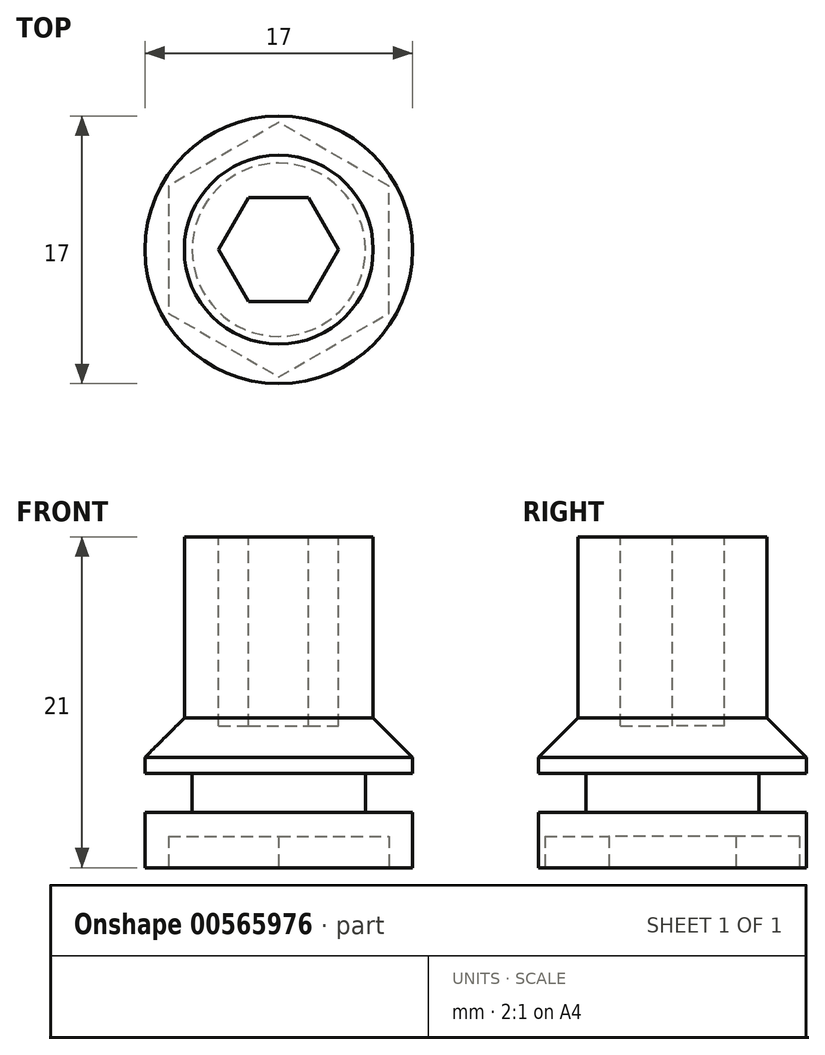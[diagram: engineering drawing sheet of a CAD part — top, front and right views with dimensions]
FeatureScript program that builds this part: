
annotation { "Feature Type Name" : "Feature", "Feature Type Description" : "" }
export const myFeature = defineFeature(function(context is Context, id is Id, definition is map)
    precondition{}
    {
        {
            var Q0;
            Q0=qCreatedBy(makeId("Top.planeOp"),FACE);
            var sketch = newSketch(context, id + "F0", { "sketchPlane" : qUnion([Q0])});
            skCircle(sketch, "E0", {"center": v(0, 0) * mm, "radius": 8.5 * mm});
            skSolve(sketch);
        }
        {
            var Q0;
            Q0=makeQuery(id+"F0.imprint","IMPRINT",FACE,{"disambiguationData":[TD([[makeQuery(id+"F0.imprint","IMPRINT",EDGE,{"derivedFrom":sQuery(id+"F0.wireOp",EDGE,"E0")}),1.0]])]});
            extrude(context, id + "F1", {"entities" : qUnion([Q0]), "depth" : 11 * mm, "offsetDistance" : 25 * mm});
        }
        {
            var Q0;
            Q0=makeQuery(id+"F1.opExtrude","CAP_FACE",FACE,{"disambiguationData":[OSD([sQuery(id+"F0.wireOp",EDGE,"E0")])],"isStart":true});
            var sketch = newSketch(context, id + "F2", { "sketchPlane" : qUnion([Q0])});
            skCircle(sketch, "E1.cCircle", {"center": v(0, 0) * mm, "radius": 7 * mm, "construction": true});
            skLineSegment(sketch, "E1.0", {"start": v(0, 8.08) * mm, "end": v(7, 4.04) * mm});
            skLineSegment(sketch, "E1.1", {"start": v(7, 4.04) * mm, "end": v(7, -4.04) * mm});
            skLineSegment(sketch, "E1.2", {"start": v(7, -4.04) * mm, "end": v(0, -8.08) * mm});
            skLineSegment(sketch, "E1.3", {"start": v(0, -8.08) * mm, "end": v(-7, -4.04) * mm});
            skLineSegment(sketch, "E1.4", {"start": v(-7, -4.04) * mm, "end": v(-7, 4.04) * mm});
            skLineSegment(sketch, "E1.5", {"start": v(-7, 4.04) * mm, "end": v(0, 8.08) * mm});
            skPoint(sketch, "E1.0.midPoint", {"position": v(3.5, 6.06) * mm});
            skSolve(sketch);
        }
        {
            var Q0;
            Q0=makeQuery(id+"F2.imprint","IMPRINT",FACE,{"disambiguationData":[TD([[makeQuery(id+"F2.imprint","IMPRINT",EDGE,{"derivedFrom":sQuery(id+"F2.wireOp",EDGE,"E1.0")}),-1.0]])]});
            extrude(context, id + "F3", {"entities" : qUnion([Q0]), "operationType" : NewBodyOperationType.REMOVE, "oppositeDirection" : true, "depth" : 2 * mm, "offsetDistance" : 25 * mm});
        }
        {
            var Q0;
            Q0=makeQuery(id+"F1.opExtrude","CAP_FACE",FACE,{"disambiguationData":[OSD([sQuery(id+"F0.wireOp",EDGE,"E0")])],"isStart":true});
            cPlane(context, id + "F4", {"entities" : qUnion([Q0]), "cplaneType" : CPlaneType.OFFSET, "offset" : 3.5 * mm, "oppositeDirection" : true, "width" : 150 * mm, "height" : 150 * mm});
        }
        {
            var Q0;
            Q0=qCreatedBy(id+"F4.planeOp",FACE);
            var sketch = newSketch(context, id + "F5", { "sketchPlane" : qUnion([Q0])});
            skCircle(sketch, "E2", {"center": v(0, 0) * mm, "radius": 8.5 * mm});
            skCircle(sketch, "E3", {"center": v(0, 0) * mm, "radius": 5.5 * mm});
            skSolve(sketch);
        }
        {
            var Q0;
            Q0 = qSketchRegion(id + "F5", true);
            extrude(context, id + "F6", {"entities" : qUnion([Q0]), "operationType" : NewBodyOperationType.REMOVE, "oppositeDirection" : true, "depth" : 2.5 * mm, "offsetDistance" : 25 * mm});
        }
        {
            var Q0;
            Q0=makeQuery(id+"F1.opExtrude","CAP_FACE",FACE,{"disambiguationData":[OSD([sQuery(id+"F0.wireOp",EDGE,"E0")])],"isStart":false});
            var sketch = newSketch(context, id + "F7", { "sketchPlane" : qUnion([Q0])});
            skCircle(sketch, "E4", {"center": v(0, 0) * mm, "radius": 6 * mm});
            skSolve(sketch);
        }
        {
            var Q0;
            Q0=makeQuery(id+"F7.imprint","IMPRINT",FACE,{"disambiguationData":[TD([[makeQuery(id+"F7.imprint","IMPRINT",EDGE,{"derivedFrom":sQuery(id+"F7.wireOp",EDGE,"E4")}),1.0]])]});
            extrude(context, id + "F8", {"entities" : qUnion([Q0]), "operationType" : NewBodyOperationType.ADD, "depth" : 10 * mm, "offsetDistance" : 25 * mm});
        }
        {
            var Q0;
            Q0=makeQuery(id+"F1.opExtrude","CAP_EDGE",EDGE,{"disambiguationData":[OSD([sQuery(id+"F0.wireOp",EDGE,"E0")])],"isStart":false});
            chamfer(context, id + "F9", {"entities" : qUnion([Q0]), "width" : 4 * mm, "tangentPropagation" : true});
        }
        {
            var Q0;
            Q0=makeQuery(id+"F8.opExtrude","CAP_FACE",FACE,{"disambiguationData":[OSD([sQuery(id+"F7.wireOp",EDGE,"E4")])],"isStart":false});
            var sketch = newSketch(context, id + "F10", { "sketchPlane" : qUnion([Q0])});
            skCircle(sketch, "E5.cCircle", {"center": v(0, 0) * mm, "radius": 3.3 * mm, "construction": true});
            skLineSegment(sketch, "E5.0", {"start": v(1.9, 3.3) * mm, "end": v(3.81, 0) * mm});
            skLineSegment(sketch, "E5.1", {"start": v(3.81, 0) * mm, "end": v(1.9, -3.3) * mm});
            skLineSegment(sketch, "E5.2", {"start": v(1.9, -3.3) * mm, "end": v(-1.9, -3.3) * mm});
            skLineSegment(sketch, "E5.3", {"start": v(-1.9, -3.3) * mm, "end": v(-3.81, 0) * mm});
            skLineSegment(sketch, "E5.4", {"start": v(-3.81, 0) * mm, "end": v(-1.9, 3.3) * mm});
            skLineSegment(sketch, "E5.5", {"start": v(-1.9, 3.3) * mm, "end": v(1.9, 3.3) * mm});
            skPoint(sketch, "E5.0.midPoint", {"position": v(2.86, 1.65) * mm});
            skSolve(sketch);
        }
        {
            var Q0;
            Q0=makeQuery(id+"F10.imprint","IMPRINT",FACE,{"disambiguationData":[TD([[makeQuery(id+"F10.imprint","IMPRINT",EDGE,{"derivedFrom":sQuery(id+"F10.wireOp",EDGE,"E5.0")}),-1.0]])]});
            extrude(context, id + "F11", {"entities" : qUnion([Q0]), "operationType" : NewBodyOperationType.REMOVE, "oppositeDirection" : true, "depth" : 12 * mm, "offsetDistance" : 25 * mm});
        }
    });
